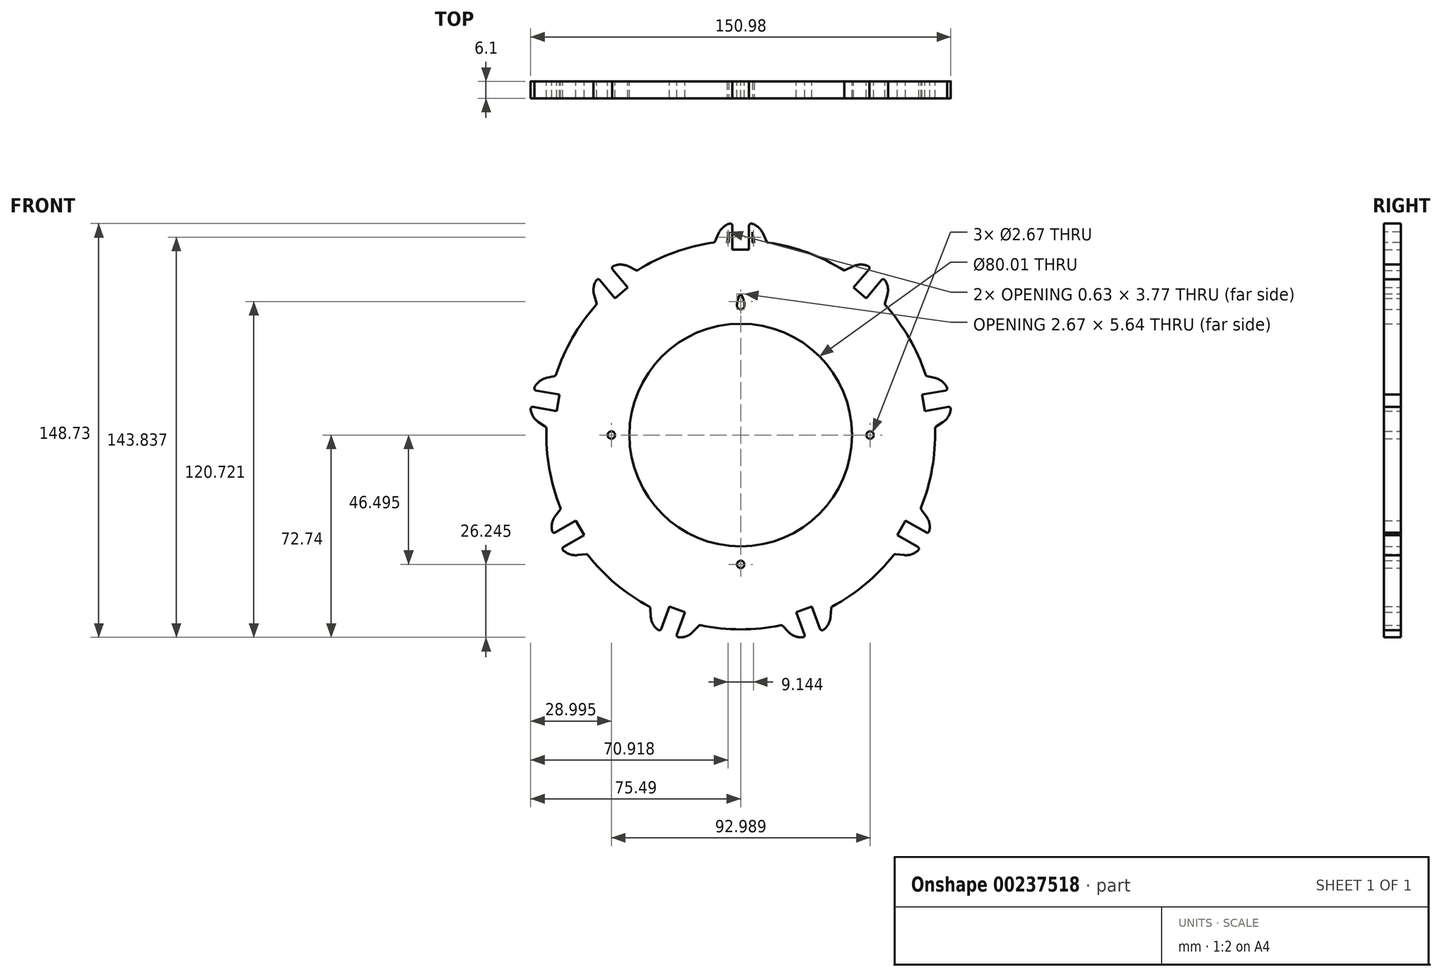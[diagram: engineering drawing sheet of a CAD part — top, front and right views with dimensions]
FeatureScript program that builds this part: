
annotation { "Feature Type Name" : "Feature", "Feature Type Description" : "" }
export const myFeature = defineFeature(function(context is Context, id is Id, definition is map)
    precondition{}
    {
        {
            var Q0;
            Q0=qCreatedBy(makeId("Front.planeOp"),FACE);
            var sketch = newSketch(context, id + "F0", { "sketchPlane" : qUnion([Q0])});
            skCircle(sketch, "E0", {"center": v(0, 0) * mm, "radius": 69.85 * mm});
            skCircle(sketch, "E1", {"center": v(0, 0) * mm, "radius": 40 * mm});
            skCircle(sketch, "E2", {"center": v(0, 0) * mm, "radius": 46.5 * mm, "construction": true});
            skPoint(sketch, "E3.center", {"position": v(0, -7.07) * mm});
            skLineSegment(sketch, "E4", {"start": v(-9.44, 69.2) * mm, "end": v(-8.02, 72.42) * mm});
            skLineSegment(sketch, "E5", {"start": v(-2.21, 76.2) * mm, "end": v(2.21, 76.2) * mm});
            skLineSegment(sketch, "E6", {"start": v(8.02, 72.42) * mm, "end": v(9.44, 69.2) * mm});
            skPoint(sketch, "E7", {"position": v(0, 76.2) * mm});
            skLineSegment(sketch, "E8", {"start": v(-9.44, 69.2) * mm, "end": v(-40, 0) * mm, "construction": true});
            skLineSegment(sketch, "E9", {"start": v(40, 0) * mm, "end": v(9.44, 69.2) * mm, "construction": true});
            skLineSegment(sketch, "E10", {"start": v(-2.98, 76.2) * mm, "end": v(-2.98, 66.67) * mm});
            skLineSegment(sketch, "E11", {"start": v(-2.98, 66.68) * mm, "end": v(2.98, 66.68) * mm});
            skLineSegment(sketch, "E12", {"start": v(2.98, 66.67) * mm, "end": v(2.98, 76.2) * mm});
            skPoint(sketch, "E13", {"position": v(0, 66.67) * mm});
            skPoint(sketch, "E14.visualSharp", {"position": v(-6.35, 76.2) * mm});
            skArc(sketch, "E14.filletArc", {"start": v(-2.21, 76.2) * mm, "mid": v(-5.68, 75.17) * mm, "end": v(-8.02, 72.42) * mm});
            skPoint(sketch, "E15.visualSharp", {"position": v(6.35, 76.2) * mm});
            skArc(sketch, "E15.filletArc", {"start": v(8.02, 72.42) * mm, "mid": v(5.68, 75.17) * mm, "end": v(2.21, 76.2) * mm});
            skCircle(sketch, "E16.MirrorC", {"center": v(0, 46.5) * mm, "radius": 1.33 * mm});
            skCircle(sketch, "E17", {"center": v(0, 0) * mm, "radius": 66.72 * mm, "construction": true});
            skCircle(sketch, "E18.1.0", {"center": v(-46.5, 0) * mm, "radius": 1.33 * mm});
            skCircle(sketch, "E18.2.0", {"center": v(0, -46.5) * mm, "radius": 1.33 * mm});
            skCircle(sketch, "E18.3.0", {"center": v(46.5, 0) * mm, "radius": 1.33 * mm});
            skCircle(sketch, "E19", {"center": v(0, 0) * mm, "radius": 50.8 * mm, "construction": true});
            skArc(sketch, "E20", {"start": v(1.33, 46.48) * mm, "mid": v(1, 48.74) * mm, "end": v(0, 50.8) * mm});
            skArc(sketch, "E21", {"start": v(0, 50.8) * mm, "mid": v(-1, 48.74) * mm, "end": v(-1.33, 46.48) * mm});
            skLineSegment(sketch, "E22.1.0", {"start": v(-51.72, 46.95) * mm, "end": v(-52.7, 50.32) * mm});
            skArc(sketch, "E22.1.1", {"start": v(-50.68, 56.95) * mm, "mid": v(-52.67, 53.93) * mm, "end": v(-52.7, 50.32) * mm});
            skLineSegment(sketch, "E22.1.2", {"start": v(-51.27, 56.45) * mm, "end": v(-45.14, 49.16) * mm});
            skLineSegment(sketch, "E22.1.3", {"start": v(-40.57, 53) * mm, "end": v(-46.7, 60.3) * mm});
            skArc(sketch, "E22.1.4", {"start": v(-40.4, 60.63) * mm, "mid": v(-43.97, 61.23) * mm, "end": v(-47.29, 59.8) * mm});
            skLineSegment(sketch, "E22.1.5", {"start": v(-40.4, 60.63) * mm, "end": v(-37.26, 59.08) * mm});
            skLineSegment(sketch, "E22.1.6", {"start": v(-45.14, 49.16) * mm, "end": v(-40.57, 53) * mm});
            skLineSegment(sketch, "E22.2.0", {"start": v(-69.8, 2.72) * mm, "end": v(-72.7, 4.68) * mm});
            skArc(sketch, "E22.2.1", {"start": v(-75.43, 11.05) * mm, "mid": v(-75.01, 7.46) * mm, "end": v(-72.7, 4.68) * mm});
            skLineSegment(sketch, "E22.2.2", {"start": v(-75.56, 10.3) * mm, "end": v(-66.18, 8.64) * mm});
            skLineSegment(sketch, "E22.2.3", {"start": v(-65.14, 14.52) * mm, "end": v(-74.52, 16.17) * mm});
            skArc(sketch, "E22.2.4", {"start": v(-69.92, 20.47) * mm, "mid": v(-73.04, 18.65) * mm, "end": v(-74.66, 15.41) * mm});
            skLineSegment(sketch, "E22.2.5", {"start": v(-69.92, 20.47) * mm, "end": v(-66.52, 21.31) * mm});
            skLineSegment(sketch, "E22.2.6", {"start": v(-66.18, 8.64) * mm, "end": v(-65.14, 14.52) * mm});
            skLineSegment(sketch, "E22.3.0", {"start": v(-55.22, -42.78) * mm, "end": v(-58.7, -43.15) * mm});
            skArc(sketch, "E22.3.1", {"start": v(-64.88, -40.02) * mm, "mid": v(-62.26, -42.5) * mm, "end": v(-58.7, -43.15) * mm});
            skLineSegment(sketch, "E22.3.2", {"start": v(-64.5, -40.68) * mm, "end": v(-56.25, -35.92) * mm});
            skLineSegment(sketch, "E22.3.3", {"start": v(-59.23, -30.75) * mm, "end": v(-67.48, -35.52) * mm});
            skArc(sketch, "E22.3.4", {"start": v(-66.72, -29.26) * mm, "mid": v(-67.94, -32.67) * mm, "end": v(-67.1, -36.18) * mm});
            skLineSegment(sketch, "E22.3.5", {"start": v(-66.72, -29.26) * mm, "end": v(-64.66, -26.43) * mm});
            skLineSegment(sketch, "E22.3.6", {"start": v(-56.25, -35.92) * mm, "end": v(-59.23, -30.75) * mm});
            skLineSegment(sketch, "E22.4.0", {"start": v(-14.8, -68.26) * mm, "end": v(-17.23, -70.8) * mm});
            skArc(sketch, "E22.4.1", {"start": v(-23.98, -72.36) * mm, "mid": v(-20.37, -72.58) * mm, "end": v(-17.23, -70.8) * mm});
            skLineSegment(sketch, "E22.4.2", {"start": v(-23.26, -72.63) * mm, "end": v(-20, -63.67) * mm});
            skLineSegment(sketch, "E22.4.3", {"start": v(-25.6, -61.63) * mm, "end": v(-28.87, -70.58) * mm});
            skArc(sketch, "E22.4.4", {"start": v(-32.3, -65.3) * mm, "mid": v(-31.05, -68.7) * mm, "end": v(-28.14, -70.85) * mm});
            skLineSegment(sketch, "E22.4.5", {"start": v(-32.3, -65.3) * mm, "end": v(-32.54, -61.8) * mm});
            skLineSegment(sketch, "E22.4.6", {"start": v(-20, -63.67) * mm, "end": v(-25.6, -61.63) * mm});
            skLineSegment(sketch, "E22.5.0", {"start": v(32.54, -61.8) * mm, "end": v(32.3, -65.3) * mm});
            skArc(sketch, "E22.5.1", {"start": v(28.14, -70.85) * mm, "mid": v(31.05, -68.7) * mm, "end": v(32.3, -65.3) * mm});
            skLineSegment(sketch, "E22.5.2", {"start": v(28.87, -70.58) * mm, "end": v(25.6, -61.63) * mm});
            skLineSegment(sketch, "E22.5.3", {"start": v(20, -63.67) * mm, "end": v(23.26, -72.63) * mm});
            skArc(sketch, "E22.5.4", {"start": v(17.23, -70.8) * mm, "mid": v(20.37, -72.58) * mm, "end": v(23.98, -72.36) * mm});
            skLineSegment(sketch, "E22.5.5", {"start": v(17.23, -70.8) * mm, "end": v(14.8, -68.26) * mm});
            skLineSegment(sketch, "E22.5.6", {"start": v(25.6, -61.63) * mm, "end": v(20, -63.67) * mm});
            skLineSegment(sketch, "E22.6.0", {"start": v(64.66, -26.43) * mm, "end": v(66.72, -29.26) * mm});
            skArc(sketch, "E22.6.1", {"start": v(67.1, -36.18) * mm, "mid": v(67.94, -32.67) * mm, "end": v(66.72, -29.26) * mm});
            skLineSegment(sketch, "E22.6.2", {"start": v(67.48, -35.52) * mm, "end": v(59.23, -30.75) * mm});
            skLineSegment(sketch, "E22.6.3", {"start": v(56.25, -35.92) * mm, "end": v(64.5, -40.68) * mm});
            skArc(sketch, "E22.6.4", {"start": v(58.7, -43.15) * mm, "mid": v(62.26, -42.5) * mm, "end": v(64.88, -40.02) * mm});
            skLineSegment(sketch, "E22.6.5", {"start": v(58.7, -43.15) * mm, "end": v(55.22, -42.78) * mm});
            skLineSegment(sketch, "E22.6.6", {"start": v(59.23, -30.75) * mm, "end": v(56.25, -35.92) * mm});
            skLineSegment(sketch, "E22.7.0", {"start": v(66.52, 21.31) * mm, "end": v(69.92, 20.47) * mm});
            skArc(sketch, "E22.7.1", {"start": v(74.66, 15.41) * mm, "mid": v(73.04, 18.65) * mm, "end": v(69.92, 20.47) * mm});
            skLineSegment(sketch, "E22.7.2", {"start": v(74.52, 16.17) * mm, "end": v(65.14, 14.52) * mm});
            skLineSegment(sketch, "E22.7.3", {"start": v(66.18, 8.64) * mm, "end": v(75.56, 10.3) * mm});
            skArc(sketch, "E22.7.4", {"start": v(72.7, 4.68) * mm, "mid": v(75.01, 7.46) * mm, "end": v(75.43, 11.05) * mm});
            skLineSegment(sketch, "E22.7.5", {"start": v(72.7, 4.68) * mm, "end": v(69.8, 2.72) * mm});
            skLineSegment(sketch, "E22.7.6", {"start": v(65.14, 14.52) * mm, "end": v(66.18, 8.64) * mm});
            skLineSegment(sketch, "E22.8.0", {"start": v(37.26, 59.08) * mm, "end": v(40.4, 60.63) * mm});
            skArc(sketch, "E22.8.1", {"start": v(47.29, 59.8) * mm, "mid": v(43.97, 61.23) * mm, "end": v(40.4, 60.63) * mm});
            skLineSegment(sketch, "E22.8.2", {"start": v(46.7, 60.3) * mm, "end": v(40.57, 53) * mm});
            skLineSegment(sketch, "E22.8.3", {"start": v(45.14, 49.16) * mm, "end": v(51.27, 56.45) * mm});
            skArc(sketch, "E22.8.4", {"start": v(52.7, 50.32) * mm, "mid": v(52.67, 53.93) * mm, "end": v(50.68, 56.95) * mm});
            skLineSegment(sketch, "E22.8.5", {"start": v(52.7, 50.32) * mm, "end": v(51.72, 46.95) * mm});
            skLineSegment(sketch, "E22.8.6", {"start": v(40.57, 53) * mm, "end": v(45.14, 49.16) * mm});
            skSolve(sketch);
        }
        {
            var Q0;
            Q0=makeQuery(id+"F0.imprint","IMPRINT",FACE,{"disambiguationData":[TD([[makeQuery(id+"F0.imprint","IMPRINT",EDGE,{"derivedFrom":sQuery(id+"F0.wireOp",EDGE,"E1")}),-1.0]])]});
            var Q1;
            {var subQ0=sQuery(id+"F0.wireOp",EDGE,"E22.1.5");Q1=makeQuery(id+"F0.imprint","IMPRINT",FACE,{"disambiguationData":[TD([[makeQuery(id+"F0.imprint","IMPRINT",EDGE,{"derivedFrom":subQ0}),-1.0]])]});}
            var Q2;
            {var subQ0=sQuery(id+"F0.wireOp",EDGE,"E22.1.0");Q2=makeQuery(id+"F0.imprint","IMPRINT",FACE,{"disambiguationData":[TD([[makeQuery(id+"F0.imprint","IMPRINT",EDGE,{"derivedFrom":subQ0}),-1.0]])]});}
            var Q3;
            {var subQ0=sQuery(id+"F0.wireOp",EDGE,"E4");Q3=makeQuery(id+"F0.imprint","IMPRINT",FACE,{"disambiguationData":[TD([[makeQuery(id+"F0.imprint","IMPRINT",EDGE,{"derivedFrom":subQ0}),-1.0]])]});}
            var Q4;
            {var subQ0=sQuery(id+"F0.wireOp",EDGE,"E6");Q4=makeQuery(id+"F0.imprint","IMPRINT",FACE,{"disambiguationData":[TD([[makeQuery(id+"F0.imprint","IMPRINT",EDGE,{"derivedFrom":subQ0}),-1.0]])]});}
            var Q5;
            {var subQ0=sQuery(id+"F0.wireOp",EDGE,"E22.8.0");Q5=makeQuery(id+"F0.imprint","IMPRINT",FACE,{"disambiguationData":[TD([[makeQuery(id+"F0.imprint","IMPRINT",EDGE,{"derivedFrom":subQ0}),-1.0]])]});}
            var Q6;
            {var subQ0=sQuery(id+"F0.wireOp",EDGE,"E22.8.5");Q6=makeQuery(id+"F0.imprint","IMPRINT",FACE,{"disambiguationData":[TD([[makeQuery(id+"F0.imprint","IMPRINT",EDGE,{"derivedFrom":subQ0}),-1.0]])]});}
            var Q7;
            {var subQ0=sQuery(id+"F0.wireOp",EDGE,"E22.7.0");Q7=makeQuery(id+"F0.imprint","IMPRINT",FACE,{"disambiguationData":[TD([[makeQuery(id+"F0.imprint","IMPRINT",EDGE,{"derivedFrom":subQ0}),-1.0]])]});}
            var Q8;
            {var subQ0=sQuery(id+"F0.wireOp",EDGE,"E22.7.5");Q8=makeQuery(id+"F0.imprint","IMPRINT",FACE,{"disambiguationData":[TD([[makeQuery(id+"F0.imprint","IMPRINT",EDGE,{"derivedFrom":subQ0}),-1.0]])]});}
            var Q9;
            {var subQ0=sQuery(id+"F0.wireOp",EDGE,"E22.6.0");Q9=makeQuery(id+"F0.imprint","IMPRINT",FACE,{"disambiguationData":[TD([[makeQuery(id+"F0.imprint","IMPRINT",EDGE,{"derivedFrom":subQ0}),-1.0]])]});}
            var Q10;
            {var subQ0=sQuery(id+"F0.wireOp",EDGE,"E22.6.5");Q10=makeQuery(id+"F0.imprint","IMPRINT",FACE,{"disambiguationData":[TD([[makeQuery(id+"F0.imprint","IMPRINT",EDGE,{"derivedFrom":subQ0}),-1.0]])]});}
            var Q11;
            {var subQ0=sQuery(id+"F0.wireOp",EDGE,"E22.5.5");Q11=makeQuery(id+"F0.imprint","IMPRINT",FACE,{"disambiguationData":[TD([[makeQuery(id+"F0.imprint","IMPRINT",EDGE,{"derivedFrom":subQ0}),-1.0]])]});}
            var Q12;
            {var subQ0=sQuery(id+"F0.wireOp",EDGE,"E22.5.0");Q12=makeQuery(id+"F0.imprint","IMPRINT",FACE,{"disambiguationData":[TD([[makeQuery(id+"F0.imprint","IMPRINT",EDGE,{"derivedFrom":subQ0}),-1.0]])]});}
            var Q13;
            {var subQ0=sQuery(id+"F0.wireOp",EDGE,"E22.4.5");Q13=makeQuery(id+"F0.imprint","IMPRINT",FACE,{"disambiguationData":[TD([[makeQuery(id+"F0.imprint","IMPRINT",EDGE,{"derivedFrom":subQ0}),-1.0]])]});}
            var Q14;
            {var subQ0=sQuery(id+"F0.wireOp",EDGE,"E22.4.0");Q14=makeQuery(id+"F0.imprint","IMPRINT",FACE,{"disambiguationData":[TD([[makeQuery(id+"F0.imprint","IMPRINT",EDGE,{"derivedFrom":subQ0}),-1.0]])]});}
            var Q15;
            {var subQ0=sQuery(id+"F0.wireOp",EDGE,"E22.3.0");Q15=makeQuery(id+"F0.imprint","IMPRINT",FACE,{"disambiguationData":[TD([[makeQuery(id+"F0.imprint","IMPRINT",EDGE,{"derivedFrom":subQ0}),-1.0]])]});}
            var Q16;
            {var subQ0=sQuery(id+"F0.wireOp",EDGE,"E22.3.5");Q16=makeQuery(id+"F0.imprint","IMPRINT",FACE,{"disambiguationData":[TD([[makeQuery(id+"F0.imprint","IMPRINT",EDGE,{"derivedFrom":subQ0}),-1.0]])]});}
            var Q17;
            {var subQ0=sQuery(id+"F0.wireOp",EDGE,"E22.2.0");Q17=makeQuery(id+"F0.imprint","IMPRINT",FACE,{"disambiguationData":[TD([[makeQuery(id+"F0.imprint","IMPRINT",EDGE,{"derivedFrom":subQ0}),-1.0]])]});}
            var Q18;
            {var subQ0=sQuery(id+"F0.wireOp",EDGE,"E22.2.5");Q18=makeQuery(id+"F0.imprint","IMPRINT",FACE,{"disambiguationData":[TD([[makeQuery(id+"F0.imprint","IMPRINT",EDGE,{"derivedFrom":subQ0}),-1.0]])]});}
            extrude(context, id + "F1", {"entities" : qUnion([Q0, Q1, Q2, Q3, Q4, Q5, Q6, Q7, Q8, Q9, Q10, Q11, Q12, Q13, Q14, Q15, Q16, Q17, Q18]), "offsetDistance" : 25.4 * mm, "depth" : 6.1 * mm});
        }
        {
            var Q0;
            {var subQ0=sQuery(id+"FvJpxpYg898pNAX_1.wireOp",EDGE,"53E3jjuS-hRJ3-EJHB-q42a-zf0OxQkTzMQm");var subQ1=sQuery(id+"FvJpxpYg898pNAX_1.wireOp",EDGE,"eDTWx6nS-4LiB-bQoC-8h4n-UFIUxgX0mG1X");var subQ2=sQuery(id+"FvJpxpYg898pNAX_1.wireOp",EDGE,"w75uQd79-OuTk-zNXF-Czll-kn5tBHbynTvD");var subQ3=sQuery(id+"FvJpxpYg898pNAX_1.wireOp",EDGE,"Ia1vBbiV-KCZw-VCwM-2Djj-mJQj9exYNCmG");var subQ4=sQuery(id+"F0.wireOp",EDGE,"E22.4.5");var subQ5=sQuery(id+"F0.wireOp",EDGE,"E22.3.6");var subQ6=sQuery(id+"F0.wireOp",EDGE,"E22.3.4");var subQ7=sQuery(id+"F0.wireOp",EDGE,"E22.4.2");var subQ8=sQuery(id+"F0.wireOp",EDGE,"E22.3.2");var subQ9=sQuery(id+"F0.wireOp",EDGE,"E22.4.4");var subQ10=sQuery(id+"F0.wireOp",EDGE,"E22.3.3");var subQ11=sQuery(id+"F0.wireOp",EDGE,"E22.3.1");var subQ12=sQuery(id+"F0.wireOp",EDGE,"E22.4.0");var subQ13=sQuery(id+"F0.wireOp",EDGE,"E22.2.6");var subQ14=sQuery(id+"F0.wireOp",EDGE,"E22.2.4");var subQ15=sQuery(id+"F0.wireOp",EDGE,"E22.2.2");var subQ16=sQuery(id+"F0.wireOp",EDGE,"E22.2.0");var subQ17=sQuery(id+"F0.wireOp",EDGE,"E22.1.2");var subQ18=sQuery(id+"F0.wireOp",EDGE,"E22.1.6");var subQ19=sQuery(id+"F0.wireOp",EDGE,"E22.5.0");var subQ20=sQuery(id+"F0.wireOp",EDGE,"E0");var subQ21=sQuery(id+"F0.wireOp",EDGE,"E22.6.5");var subQ22=sQuery(id+"F0.wireOp",EDGE,"E22.6.1");var subQ23=sQuery(id+"F0.wireOp",EDGE,"E12");var subQ24=sQuery(id+"F0.wireOp",EDGE,"E22.5.5");var subQ25=sQuery(id+"F0.wireOp",EDGE,"E22.3.0");var subQ26=sQuery(id+"F0.wireOp",EDGE,"E22.7.5");var subQ27=sQuery(id+"F0.wireOp",EDGE,"E22.3.5");var subQ28=sQuery(id+"F0.wireOp",EDGE,"E22.4.3");var subQ29=sQuery(id+"F0.wireOp",EDGE,"E22.8.5");var subQ30=sQuery(id+"F0.wireOp",EDGE,"E22.7.0");var subQ31=sQuery(id+"F0.wireOp",EDGE,"E22.1.1");var subQ32=sQuery(id+"F0.wireOp",EDGE,"E22.8.4");var subQ33=sQuery(id+"F0.wireOp",EDGE,"E14.filletArc");var subQ34=sQuery(id+"F0.wireOp",EDGE,"E22.6.0");var subQ35=sQuery(id+"F0.wireOp",EDGE,"E22.1.3");var subQ36=sQuery(id+"F0.wireOp",EDGE,"E22.8.6");var subQ37=sQuery(id+"F0.wireOp",EDGE,"E6");var subQ38=sQuery(id+"F0.wireOp",EDGE,"E22.8.0");var subQ39=sQuery(id+"F0.wireOp",EDGE,"E22.7.1");var subQ40=sQuery(id+"F0.wireOp",EDGE,"E4");var subQ41=sQuery(id+"F0.wireOp",EDGE,"E22.1.5");var subQ42=sQuery(id+"F0.wireOp",EDGE,"E22.6.4");var subQ43=sQuery(id+"F0.wireOp",EDGE,"E22.5.1");var subQ44=sQuery(id+"F0.wireOp",EDGE,"E22.4.6");var subQ45=sQuery(id+"F0.wireOp",EDGE,"E22.1.0");var subQ46=sQuery(id+"F0.wireOp",EDGE,"E22.2.5");var subQ47=sQuery(id+"F0.wireOp",EDGE,"E10");var subQ48=sQuery(id+"F0.wireOp",EDGE,"E22.6.6");var subQ49=sQuery(id+"F0.wireOp",EDGE,"E11");var subQ50=sQuery(id+"F0.wireOp",EDGE,"E15.filletArc");var subQ51=sQuery(id+"F0.wireOp",EDGE,"E22.2.3");var subQ52=sQuery(id+"F0.wireOp",EDGE,"E22.2.1");var subQ53=sQuery(id+"F0.wireOp",EDGE,"E22.4.1");var subQ54=sQuery(id+"F0.wireOp",EDGE,"E22.1.4");var subQ55=sQuery(id+"F0.wireOp",EDGE,"E22.5.2");var subQ56=sQuery(id+"F0.wireOp",EDGE,"E22.8.3");var subQ57=sQuery(id+"F0.wireOp",EDGE,"E22.5.3");var subQ58=sQuery(id+"F0.wireOp",EDGE,"E22.5.4");var subQ59=sQuery(id+"F0.wireOp",EDGE,"E22.5.6");var subQ60=sQuery(id+"F0.wireOp",EDGE,"E22.6.2");var subQ61=sQuery(id+"F0.wireOp",EDGE,"E22.6.3");var subQ62=sQuery(id+"F0.wireOp",EDGE,"E22.7.2");var subQ63=sQuery(id+"F0.wireOp",EDGE,"E22.7.3");var subQ64=sQuery(id+"F0.wireOp",EDGE,"E22.7.4");var subQ65=sQuery(id+"F0.wireOp",EDGE,"E22.7.6");var subQ66=sQuery(id+"F0.wireOp",EDGE,"E22.8.1");var subQ67=sQuery(id+"F0.wireOp",EDGE,"E22.8.2");Q0=makeQuery(id+"Fi6H0UMDYzaO5z0_1.1.FCaG3GybYMWkdXD_1.boolean.opBoolean","MERGE",FACE,{"derivedFrom":[makeQuery(id+"FCaG3GybYMWkdXD_1.boolean.opBoolean","MERGE",FACE,{"derivedFrom":[makeQuery(id+"FytycAvAVJUMnGM_1.boolean.opBoolean","SPLIT",FACE,{"disambiguationData":[TD([makeQuery(id+"F1.opExtrude","SWEPT_FACE",FACE,{"disambiguationData":[OSD([subQ40])]})])],"derivedFrom":makeQuery(id+"F1.opExtrude","CAP_FACE",FACE,{"disambiguationData":[OSD([subQ20,sQuery(id+"F0.wireOp",EDGE,"E1"),subQ40,subQ37,subQ47,subQ49,subQ23,subQ33,subQ50,sQuery(id+"F0.wireOp",EDGE,"E16.MirrorC"),sQuery(id+"F0.wireOp",EDGE,"E18.1.0"),sQuery(id+"F0.wireOp",EDGE,"E18.2.0"),sQuery(id+"F0.wireOp",EDGE,"E18.3.0"),sQuery(id+"F0.wireOp",EDGE,"E20"),sQuery(id+"F0.wireOp",EDGE,"E21"),subQ45,subQ31,subQ17,subQ35,subQ54,subQ41,subQ18,subQ16,subQ52,subQ15,subQ51,subQ14,subQ46,subQ13,subQ25,subQ11,subQ8,subQ10,subQ6,subQ27,subQ5,subQ12,subQ53,subQ7,subQ28,subQ9,subQ4,subQ44,subQ19,subQ43,subQ55,subQ57,subQ58,subQ24,subQ59,subQ34,subQ22,subQ60,subQ61,subQ42,subQ21,subQ48,subQ30,subQ39,subQ62,subQ63,subQ64,subQ26,subQ65,subQ38,subQ66,subQ67,subQ56,subQ32,subQ29,subQ36])],"isStart":false})}),makeQuery(id+"FCaG3GybYMWkdXD_1.opExtrude","CAP_FACE",FACE,{"disambiguationData":[OSD([subQ3,subQ2,subQ1,subQ0])],"isStart":true})]}),makeQuery(id+"Fi6H0UMDYzaO5z0_1.1.FCaG3GybYMWkdXD_1.opExtrude","CAP_FACE",FACE,{"disambiguationData":[OSD([subQ3,subQ2,subQ1,subQ0])],"isStart":true})]});}
            var sketch = newSketch(context, id + "F2", { "sketchPlane" : qUnion([Q0])});
            skLineSegment(sketch, "E23", {"start": v(-4.25, 72.98) * mm, "end": v(-4.25, 69.2) * mm});
            skLineSegment(sketch, "E24", {"start": v(4.25, 72.98) * mm, "end": v(4.25, 69.2) * mm});
            skLineSegment(sketch, "E25", {"start": v(4.25, 69.2) * mm, "end": v(4.89, 69.2) * mm});
            skLineSegment(sketch, "E26", {"start": v(-4.25, 69.2) * mm, "end": v(-4.89, 69.2) * mm});
            skLineSegment(sketch, "E27", {"start": v(-4.25, 72.98) * mm, "end": v(-4.89, 69.2) * mm});
            skLineSegment(sketch, "E28", {"start": v(4.25, 72.98) * mm, "end": v(4.89, 69.2) * mm});
            skLineSegment(sketch, "E29", {"start": v(-6.35, 76.2) * mm, "end": v(-4.25, 72.98) * mm, "construction": true});
            skLineSegment(sketch, "E30", {"start": v(6.35, 76.2) * mm, "end": v(4.25, 72.98) * mm, "construction": true});
            skSolve(sketch);
        }
        {
            var Q0;
            Q0=makeQuery(id+"F2.imprint","IMPRINT",FACE,{"disambiguationData":[TD([[makeQuery(id+"F2.imprint","IMPRINT",EDGE,{"derivedFrom":sQuery(id+"F2.wireOp",EDGE,"E23")}),-1.0]])]});
            var Q1;
            Q1=makeQuery(id+"F2.imprint","IMPRINT",FACE,{"disambiguationData":[TD([[makeQuery(id+"F2.imprint","IMPRINT",EDGE,{"derivedFrom":sQuery(id+"F2.wireOp",EDGE,"E24")}),1.0]])]});
            var Q2;
            Q2=makeQuery(id+"F1.opExtrude","CAP_FACE",FACE,{"disambiguationData":[OSD([sQuery(id+"F0.wireOp",EDGE,"E0"),sQuery(id+"F0.wireOp",EDGE,"E1"),sQuery(id+"F0.wireOp",EDGE,"E4"),sQuery(id+"F0.wireOp",EDGE,"E6"),sQuery(id+"F0.wireOp",EDGE,"E10"),sQuery(id+"F0.wireOp",EDGE,"E11"),sQuery(id+"F0.wireOp",EDGE,"E12"),sQuery(id+"F0.wireOp",EDGE,"E14.filletArc"),sQuery(id+"F0.wireOp",EDGE,"E15.filletArc"),sQuery(id+"F0.wireOp",EDGE,"E16.MirrorC"),sQuery(id+"F0.wireOp",EDGE,"E18.1.0"),sQuery(id+"F0.wireOp",EDGE,"E18.2.0"),sQuery(id+"F0.wireOp",EDGE,"E18.3.0"),sQuery(id+"F0.wireOp",EDGE,"E20"),sQuery(id+"F0.wireOp",EDGE,"E21"),sQuery(id+"F0.wireOp",EDGE,"E22.1.0"),sQuery(id+"F0.wireOp",EDGE,"E22.1.1"),sQuery(id+"F0.wireOp",EDGE,"E22.1.2"),sQuery(id+"F0.wireOp",EDGE,"E22.1.3"),sQuery(id+"F0.wireOp",EDGE,"E22.1.4"),sQuery(id+"F0.wireOp",EDGE,"E22.1.5"),sQuery(id+"F0.wireOp",EDGE,"E22.1.6"),sQuery(id+"F0.wireOp",EDGE,"E22.2.0"),sQuery(id+"F0.wireOp",EDGE,"E22.2.1"),sQuery(id+"F0.wireOp",EDGE,"E22.2.2"),sQuery(id+"F0.wireOp",EDGE,"E22.2.3"),sQuery(id+"F0.wireOp",EDGE,"E22.2.4"),sQuery(id+"F0.wireOp",EDGE,"E22.2.5"),sQuery(id+"F0.wireOp",EDGE,"E22.2.6"),sQuery(id+"F0.wireOp",EDGE,"E22.3.0"),sQuery(id+"F0.wireOp",EDGE,"E22.3.1"),sQuery(id+"F0.wireOp",EDGE,"E22.3.2"),sQuery(id+"F0.wireOp",EDGE,"E22.3.3"),sQuery(id+"F0.wireOp",EDGE,"E22.3.4"),sQuery(id+"F0.wireOp",EDGE,"E22.3.5"),sQuery(id+"F0.wireOp",EDGE,"E22.3.6"),sQuery(id+"F0.wireOp",EDGE,"E22.4.0"),sQuery(id+"F0.wireOp",EDGE,"E22.4.1"),sQuery(id+"F0.wireOp",EDGE,"E22.4.2"),sQuery(id+"F0.wireOp",EDGE,"E22.4.3"),sQuery(id+"F0.wireOp",EDGE,"E22.4.4"),sQuery(id+"F0.wireOp",EDGE,"E22.4.5"),sQuery(id+"F0.wireOp",EDGE,"E22.4.6"),sQuery(id+"F0.wireOp",EDGE,"E22.5.0"),sQuery(id+"F0.wireOp",EDGE,"E22.5.1"),sQuery(id+"F0.wireOp",EDGE,"E22.5.2"),sQuery(id+"F0.wireOp",EDGE,"E22.5.3"),sQuery(id+"F0.wireOp",EDGE,"E22.5.4"),sQuery(id+"F0.wireOp",EDGE,"E22.5.5"),sQuery(id+"F0.wireOp",EDGE,"E22.5.6"),sQuery(id+"F0.wireOp",EDGE,"E22.6.0"),sQuery(id+"F0.wireOp",EDGE,"E22.6.1"),sQuery(id+"F0.wireOp",EDGE,"E22.6.2"),sQuery(id+"F0.wireOp",EDGE,"E22.6.3"),sQuery(id+"F0.wireOp",EDGE,"E22.6.4"),sQuery(id+"F0.wireOp",EDGE,"E22.6.5"),sQuery(id+"F0.wireOp",EDGE,"E22.6.6"),sQuery(id+"F0.wireOp",EDGE,"E22.7.0"),sQuery(id+"F0.wireOp",EDGE,"E22.7.1"),sQuery(id+"F0.wireOp",EDGE,"E22.7.2"),sQuery(id+"F0.wireOp",EDGE,"E22.7.3"),sQuery(id+"F0.wireOp",EDGE,"E22.7.4"),sQuery(id+"F0.wireOp",EDGE,"E22.7.5"),sQuery(id+"F0.wireOp",EDGE,"E22.7.6"),sQuery(id+"F0.wireOp",EDGE,"E22.8.0"),sQuery(id+"F0.wireOp",EDGE,"E22.8.1"),sQuery(id+"F0.wireOp",EDGE,"E22.8.2"),sQuery(id+"F0.wireOp",EDGE,"E22.8.3"),sQuery(id+"F0.wireOp",EDGE,"E22.8.4"),sQuery(id+"F0.wireOp",EDGE,"E22.8.5"),sQuery(id+"F0.wireOp",EDGE,"E22.8.6")])],"isStart":true});
            extrude(context, id + "F3", {"entities" : qUnion([Q0, Q1]), "operationType" : NewBodyOperationType.REMOVE, "endBound" : BoundingType.UP_TO_SURFACE, "oppositeDirection" : true, "endBoundEntityFace" : qUnion([Q2]), "depth" : 25.4 * mm});
        }
        {
            var Q0;
            Q0=makeQuery(id+"F1.opExtrude","SWEPT_EDGE",EDGE,{"disambiguationData":[OSD([sQuery(id+"F0.wireOp",EDGE,"E10"),sQuery(id+"F0.wireOp",EDGE,"E14.filletArc")])]});
            var Q1;
            Q1=makeQuery(id+"F1.opExtrude","SWEPT_EDGE",EDGE,{"disambiguationData":[OSD([sQuery(id+"F0.wireOp",EDGE,"E12"),sQuery(id+"F0.wireOp",EDGE,"E15.filletArc")])]});
            var Q2;
            Q2=makeQuery(id+"F1.opExtrude","SWEPT_EDGE",EDGE,{"disambiguationData":[OSD([sQuery(id+"F0.wireOp",EDGE,"E22.8.1"),sQuery(id+"F0.wireOp",EDGE,"E22.8.2")])]});
            var Q3;
            Q3=makeQuery(id+"F1.opExtrude","SWEPT_EDGE",EDGE,{"disambiguationData":[OSD([sQuery(id+"F0.wireOp",EDGE,"E22.8.3"),sQuery(id+"F0.wireOp",EDGE,"E22.8.4")])]});
            var Q4;
            Q4=makeQuery(id+"F1.opExtrude","SWEPT_EDGE",EDGE,{"disambiguationData":[OSD([sQuery(id+"F0.wireOp",EDGE,"E0"),sQuery(id+"F0.wireOp",EDGE,"E6")])]});
            var Q5;
            Q5=makeQuery(id+"F1.opExtrude","SWEPT_EDGE",EDGE,{"disambiguationData":[OSD([sQuery(id+"F0.wireOp",EDGE,"E0"),sQuery(id+"F0.wireOp",EDGE,"E4")])]});
            var Q6;
            Q6=makeQuery(id+"F1.opExtrude","SWEPT_EDGE",EDGE,{"disambiguationData":[OSD([sQuery(id+"F0.wireOp",EDGE,"E22.1.3"),sQuery(id+"F0.wireOp",EDGE,"E22.1.4")])]});
            var Q7;
            Q7=makeQuery(id+"F1.opExtrude","SWEPT_EDGE",EDGE,{"disambiguationData":[OSD([sQuery(id+"F0.wireOp",EDGE,"E0"),sQuery(id+"F0.wireOp",EDGE,"E22.1.5")])]});
            var Q8;
            Q8=makeQuery(id+"F1.opExtrude","SWEPT_EDGE",EDGE,{"disambiguationData":[OSD([sQuery(id+"F0.wireOp",EDGE,"E22.1.1"),sQuery(id+"F0.wireOp",EDGE,"E22.1.2")])]});
            var Q9;
            Q9=makeQuery(id+"F1.opExtrude","SWEPT_EDGE",EDGE,{"disambiguationData":[OSD([sQuery(id+"F0.wireOp",EDGE,"E0"),sQuery(id+"F0.wireOp",EDGE,"E22.1.0")])]});
            var Q10;
            Q10=makeQuery(id+"F1.opExtrude","SWEPT_EDGE",EDGE,{"disambiguationData":[OSD([sQuery(id+"F0.wireOp",EDGE,"E0"),sQuery(id+"F0.wireOp",EDGE,"E22.2.5")])]});
            var Q11;
            Q11=makeQuery(id+"F1.opExtrude","SWEPT_EDGE",EDGE,{"disambiguationData":[OSD([sQuery(id+"F0.wireOp",EDGE,"E22.2.3"),sQuery(id+"F0.wireOp",EDGE,"E22.2.4")])]});
            var Q12;
            Q12=makeQuery(id+"F1.opExtrude","SWEPT_EDGE",EDGE,{"disambiguationData":[OSD([sQuery(id+"F0.wireOp",EDGE,"E22.2.1"),sQuery(id+"F0.wireOp",EDGE,"E22.2.2")])]});
            var Q13;
            Q13=makeQuery(id+"F1.opExtrude","SWEPT_EDGE",EDGE,{"disambiguationData":[OSD([sQuery(id+"F0.wireOp",EDGE,"E0"),sQuery(id+"F0.wireOp",EDGE,"E22.2.0")])]});
            var Q14;
            Q14=makeQuery(id+"F1.opExtrude","SWEPT_EDGE",EDGE,{"disambiguationData":[OSD([sQuery(id+"F0.wireOp",EDGE,"E0"),sQuery(id+"F0.wireOp",EDGE,"E22.3.5")])]});
            var Q15;
            Q15=makeQuery(id+"F1.opExtrude","SWEPT_EDGE",EDGE,{"disambiguationData":[OSD([sQuery(id+"F0.wireOp",EDGE,"E22.3.3"),sQuery(id+"F0.wireOp",EDGE,"E22.3.4")])]});
            var Q16;
            Q16=makeQuery(id+"F1.opExtrude","SWEPT_EDGE",EDGE,{"disambiguationData":[OSD([sQuery(id+"F0.wireOp",EDGE,"E22.3.1"),sQuery(id+"F0.wireOp",EDGE,"E22.3.2")])]});
            var Q17;
            Q17=makeQuery(id+"F1.opExtrude","SWEPT_EDGE",EDGE,{"disambiguationData":[OSD([sQuery(id+"F0.wireOp",EDGE,"E0"),sQuery(id+"F0.wireOp",EDGE,"E22.3.0")])]});
            var Q18;
            Q18=makeQuery(id+"F1.opExtrude","SWEPT_EDGE",EDGE,{"disambiguationData":[OSD([sQuery(id+"F0.wireOp",EDGE,"E0"),sQuery(id+"F0.wireOp",EDGE,"E22.4.5")])]});
            var Q19;
            Q19=makeQuery(id+"F1.opExtrude","SWEPT_EDGE",EDGE,{"disambiguationData":[OSD([sQuery(id+"F0.wireOp",EDGE,"E22.4.3"),sQuery(id+"F0.wireOp",EDGE,"E22.4.4")])]});
            var Q20;
            Q20=makeQuery(id+"F1.opExtrude","SWEPT_EDGE",EDGE,{"disambiguationData":[OSD([sQuery(id+"F0.wireOp",EDGE,"E22.4.1"),sQuery(id+"F0.wireOp",EDGE,"E22.4.2")])]});
            var Q21;
            Q21=makeQuery(id+"F1.opExtrude","SWEPT_EDGE",EDGE,{"disambiguationData":[OSD([sQuery(id+"F0.wireOp",EDGE,"E0"),sQuery(id+"F0.wireOp",EDGE,"E22.4.0")])]});
            var Q22;
            Q22=makeQuery(id+"F1.opExtrude","SWEPT_EDGE",EDGE,{"disambiguationData":[OSD([sQuery(id+"F0.wireOp",EDGE,"E0"),sQuery(id+"F0.wireOp",EDGE,"E22.5.5")])]});
            var Q23;
            Q23=makeQuery(id+"F1.opExtrude","SWEPT_EDGE",EDGE,{"disambiguationData":[OSD([sQuery(id+"F0.wireOp",EDGE,"E22.5.3"),sQuery(id+"F0.wireOp",EDGE,"E22.5.4")])]});
            var Q24;
            Q24=makeQuery(id+"F1.opExtrude","SWEPT_EDGE",EDGE,{"disambiguationData":[OSD([sQuery(id+"F0.wireOp",EDGE,"E22.5.1"),sQuery(id+"F0.wireOp",EDGE,"E22.5.2")])]});
            var Q25;
            Q25=makeQuery(id+"F1.opExtrude","SWEPT_EDGE",EDGE,{"disambiguationData":[OSD([sQuery(id+"F0.wireOp",EDGE,"E0"),sQuery(id+"F0.wireOp",EDGE,"E22.5.0")])]});
            var Q26;
            Q26=makeQuery(id+"F1.opExtrude","SWEPT_EDGE",EDGE,{"disambiguationData":[OSD([sQuery(id+"F0.wireOp",EDGE,"E22.6.3"),sQuery(id+"F0.wireOp",EDGE,"E22.6.4")])]});
            var Q27;
            Q27=makeQuery(id+"F1.opExtrude","SWEPT_EDGE",EDGE,{"disambiguationData":[OSD([sQuery(id+"F0.wireOp",EDGE,"E0"),sQuery(id+"F0.wireOp",EDGE,"E22.6.5")])]});
            var Q28;
            Q28=makeQuery(id+"F1.opExtrude","SWEPT_EDGE",EDGE,{"disambiguationData":[OSD([sQuery(id+"F0.wireOp",EDGE,"E22.6.1"),sQuery(id+"F0.wireOp",EDGE,"E22.6.2")])]});
            var Q29;
            Q29=makeQuery(id+"F1.opExtrude","SWEPT_EDGE",EDGE,{"disambiguationData":[OSD([sQuery(id+"F0.wireOp",EDGE,"E0"),sQuery(id+"F0.wireOp",EDGE,"E22.6.0")])]});
            var Q30;
            Q30=makeQuery(id+"F1.opExtrude","SWEPT_EDGE",EDGE,{"disambiguationData":[OSD([sQuery(id+"F0.wireOp",EDGE,"E0"),sQuery(id+"F0.wireOp",EDGE,"E22.7.5")])]});
            var Q31;
            Q31=makeQuery(id+"F1.opExtrude","SWEPT_EDGE",EDGE,{"disambiguationData":[OSD([sQuery(id+"F0.wireOp",EDGE,"E22.7.3"),sQuery(id+"F0.wireOp",EDGE,"E22.7.4")])]});
            var Q32;
            Q32=makeQuery(id+"F1.opExtrude","SWEPT_EDGE",EDGE,{"disambiguationData":[OSD([sQuery(id+"F0.wireOp",EDGE,"E22.7.1"),sQuery(id+"F0.wireOp",EDGE,"E22.7.2")])]});
            var Q33;
            Q33=makeQuery(id+"F1.opExtrude","SWEPT_EDGE",EDGE,{"disambiguationData":[OSD([sQuery(id+"F0.wireOp",EDGE,"E0"),sQuery(id+"F0.wireOp",EDGE,"E22.7.0")])]});
            var Q34;
            Q34=makeQuery(id+"F1.opExtrude","SWEPT_EDGE",EDGE,{"disambiguationData":[OSD([sQuery(id+"F0.wireOp",EDGE,"E0"),sQuery(id+"F0.wireOp",EDGE,"E22.8.5")])]});
            fillet(context, id + "F4", {"entities" : qUnion([Q0, Q1, Q2, Q3, Q4, Q5, Q6, Q7, Q8, Q9, Q10, Q11, Q12, Q13, Q14, Q15, Q16, Q17, Q18, Q19, Q20, Q21, Q22, Q23, Q24, Q25, Q26, Q27, Q28, Q29, Q30, Q31, Q32, Q33, Q34]), "radius" : 0.76 * mm, "tangentPropagation" : true, "allowEdgeOverflow" : false});
        }
    });
